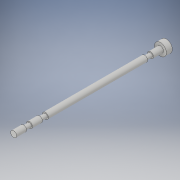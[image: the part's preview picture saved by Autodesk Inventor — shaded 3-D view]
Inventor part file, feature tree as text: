
AUTODESK INVENTOR PART (.ipt)
format: ipt  version: 2019 (Build 230136000, 136)  size: 125,952 bytes
history: native  units: mm
features: extrude x8, sketch x8
ambient origin geometry x8: Origin, YZ Plane, XZ Plane, XY Plane, X Axis, Y Axis, Z Axis, Center Point
bodies: Solid1 (feature_tree)
feature tree (16):
  extrude  "Extrusion1"  Depth=3.0mm TaperAngle=0.0deg
  extrude  "Extrusion3"  Depth=5.0mm TaperAngle=0.0deg
  extrude  "Extrusion4"  Depth=3.0mm TaperAngle=0.0deg
  extrude  "Extrusion5"  Depth=50.0mm TaperAngle=0.0deg
  extrude  "Extrusion6"  Depth=3.0mm TaperAngle=0.0deg
  extrude  "Extrusion7"  Depth=5.0mm TaperAngle=0.0deg
  extrude  "Extrusion8"  Depth=3.0mm TaperAngle=0.0deg
  extrude  "Extrusion9"  Depth=5.0mm TaperAngle=0.0deg
  sketch  "Sketch1"  dims[d0=6.0mm d1=3.0mm d2=0.0mm]
  sketch  "Sketch5"  dims[d6=3.0mm d7=5.0mm d8=0.0mm]
  sketch  "Sketch6"  dims[d9=2.0mm d10=3.0mm d11=0.0mm]
  sketch  "Sketch7"  dims[d12=3.0mm d13=50.0mm d14=0.0mm]
  sketch  "Sketch8"  dims[d15=2.0mm d16=3.0mm d17=0.0mm]
  sketch  "Sketch9"  dims[d18=3.0mm d19=5.0mm d20=0.0mm]
  sketch  "Sketch10"  dims[d21=2.0mm d22=3.0mm d23=0.0mm]
  sketch  "Sketch11"  dims[d24=3.0mm d25=5.0mm d26=0.0mm]
